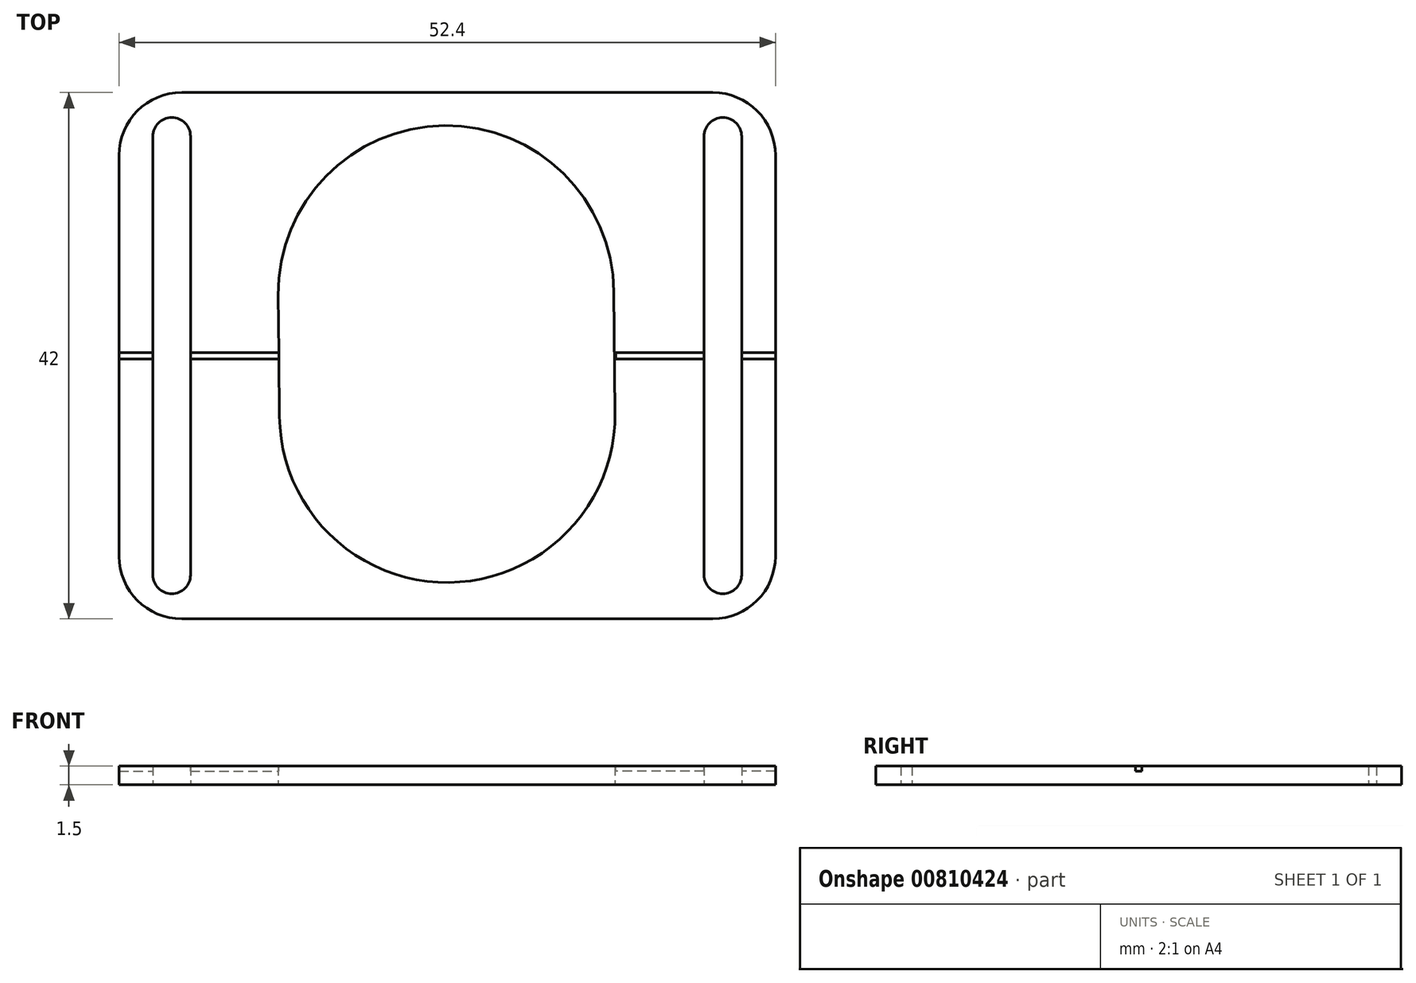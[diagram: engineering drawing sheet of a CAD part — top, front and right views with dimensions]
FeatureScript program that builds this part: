
annotation { "Feature Type Name" : "Feature", "Feature Type Description" : "" }
export const myFeature = defineFeature(function(context is Context, id is Id, definition is map)
    precondition{}
    {
        {
            var Q0;
            Q0=qCreatedBy(makeId("Top.planeOp"),FACE);
            var sketch = newSketch(context, id + "F0", { "sketchPlane" : qUnion([Q0])});
            skPoint(sketch, "E0.0", {"position": v(-35, -49.5) * mm});
            skPoint(sketch, "E1.0", {"position": v(35, -49.5) * mm});
            skLineSegment(sketch, "E2", {"start": v(-35, 25.5) * mm, "end": v(35, 25.5) * mm, "construction": true});
            skLineSegment(sketch, "E3.bottom", {"start": v(-32, -49.5) * mm, "end": v(-22, -49.5) * mm});
            skLineSegment(sketch, "E3.left", {"start": v(-35, -46.5) * mm, "end": v(-35, -44.8) * mm});
            skLineSegment(sketch, "E3.right", {"start": v(-19, -46.5) * mm, "end": v(-19, -45.44) * mm});
            skLineSegment(sketch, "E4.bottom", {"start": v(32, -49.5) * mm, "end": v(22, -49.5) * mm});
            skLineSegment(sketch, "E4.left", {"start": v(35, -46.5) * mm, "end": v(35, -44.8) * mm});
            skLineSegment(sketch, "E4.right", {"start": v(19, -46.5) * mm, "end": v(19, -45.44) * mm});
            skPoint(sketch, "E5.0", {"position": v(-19.7, -19.3) * mm});
            skPoint(sketch, "E6.0", {"position": v(19.7, -19.3) * mm});
            skArc(sketch, "E7", {"start": v(-30.65, -39.5) * mm, "mid": v(-31.62, -41.02) * mm, "end": v(-33.12, -42.02) * mm});
            skLineSegment(sketch, "E8", {"start": v(-18.8, -44.37) * mm, "end": v(-13.23, -29.76) * mm});
            skPoint(sketch, "E9.MirrorP", {"position": v(19.2, -19.2) * mm});
            skArc(sketch, "E10.MirrorCS", {"start": v(30.65, -39.5) * mm, "mid": v(31.62, -41.02) * mm, "end": v(33.12, -42.02) * mm});
            skLineSegment(sketch, "E11.MirrorCS", {"start": v(18.8, -44.37) * mm, "end": v(13.23, -29.76) * mm});
            skPoint(sketch, "E12.orphan", {"position": v(19, -39.5) * mm});
            skPoint(sketch, "E13.orphan", {"position": v(-19, -39.5) * mm});
            skPoint(sketch, "E14.visualSharp", {"position": v(-35, -42.32) * mm});
            skArc(sketch, "E14.filletArc", {"start": v(-33.12, -42.02) * mm, "mid": v(-34.48, -43.12) * mm, "end": v(-35, -44.8) * mm});
            skPoint(sketch, "E15.visualSharp", {"position": v(35, -42.32) * mm});
            skArc(sketch, "E15.filletArc", {"start": v(35, -44.8) * mm, "mid": v(34.48, -43.12) * mm, "end": v(33.12, -42.02) * mm});
            skArc(sketch, "E16.filletArc", {"start": v(32, -49.5) * mm, "mid": v(34.12, -48.62) * mm, "end": v(35, -46.5) * mm});
            skPoint(sketch, "E17.visualSharp", {"position": v(19, -49.5) * mm});
            skArc(sketch, "E17.filletArc", {"start": v(19, -46.5) * mm, "mid": v(19.88, -48.62) * mm, "end": v(22, -49.5) * mm});
            skPoint(sketch, "E18.visualSharp", {"position": v(-19, -49.5) * mm});
            skArc(sketch, "E18.filletArc", {"start": v(-22, -49.5) * mm, "mid": v(-19.88, -48.62) * mm, "end": v(-19, -46.5) * mm});
            skArc(sketch, "E19.filletArc", {"start": v(-35, -46.5) * mm, "mid": v(-34.12, -48.62) * mm, "end": v(-32, -49.5) * mm});
            skPoint(sketch, "E20.visualSharp", {"position": v(-19, -44.89) * mm});
            skArc(sketch, "E20.filletArc", {"start": v(-18.8, -44.37) * mm, "mid": v(-18.95, -44.9) * mm, "end": v(-19, -45.44) * mm});
            skPoint(sketch, "E21.visualSharp", {"position": v(19, -44.89) * mm});
            skArc(sketch, "E21.filletArc", {"start": v(19, -45.44) * mm, "mid": v(18.95, -44.9) * mm, "end": v(18.8, -44.37) * mm});
            skPoint(sketch, "E22.0", {"position": v(-32, 22.5) * mm});
            skPoint(sketch, "E23.0", {"position": v(-22, 22.5) * mm});
            skPoint(sketch, "E24.0", {"position": v(22, 22.5) * mm});
            skPoint(sketch, "E25.0", {"position": v(32, 22.5) * mm});
            skLineSegment(sketch, "E26.bottom", {"start": v(-32, 25.5) * mm, "end": v(-22, 25.5) * mm});
            skLineSegment(sketch, "E26.left", {"start": v(-35, 22.32) * mm, "end": v(-34.9, 20.58) * mm});
            skArc(sketch, "E27.filletArc", {"start": v(-34.9, 20.58) * mm, "mid": v(-34.34, 19.02) * mm, "end": v(-33.05, 18) * mm});
            skArc(sketch, "E28.filletArc", {"start": v(-32, 25.5) * mm, "mid": v(-34.18, 24.56) * mm, "end": v(-35, 22.32) * mm});
            skArc(sketch, "E29.filletArc", {"start": v(-19.63, 24.33) * mm, "mid": v(-20.68, 25.19) * mm, "end": v(-22, 25.5) * mm});
            skLineSegment(sketch, "E30", {"start": v(-33.05, 18) * mm, "end": v(-29.27, 16.41) * mm});
            skLineSegment(sketch, "E31.MirrorCS", {"start": v(35, 22.32) * mm, "end": v(34.9, 20.58) * mm});
            skArc(sketch, "E32.MirrorCS", {"start": v(19.63, 24.33) * mm, "mid": v(20.68, 25.19) * mm, "end": v(22, 25.5) * mm});
            skArc(sketch, "E33.MirrorCS", {"start": v(34.9, 20.58) * mm, "mid": v(34.34, 19.02) * mm, "end": v(33.05, 18) * mm});
            skArc(sketch, "E34.MirrorCS", {"start": v(32, 25.5) * mm, "mid": v(34.18, 24.56) * mm, "end": v(35, 22.32) * mm});
            skLineSegment(sketch, "E35.MirrorCS", {"start": v(32, 25.5) * mm, "end": v(22, 25.5) * mm});
            skLineSegment(sketch, "E36.MirrorCS", {"start": v(33.05, 18) * mm, "end": v(29.27, 16.41) * mm});
            skLineSegment(sketch, "E37", {"start": v(-15.68, 22.4) * mm, "end": v(15.68, 22.4) * mm});
            skLineSegment(sketch, "E38", {"start": v(-26.2, -26.85) * mm, "end": v(-26.2, 11.8) * mm});
            skLineSegment(sketch, "E39", {"start": v(-32, 22.5) * mm, "end": v(-22, 22.5) * mm, "construction": true});
            skCircle(sketch, "E40", {"center": v(-32, 22.5) * mm, "radius": 1.5 * mm});
            skCircle(sketch, "E41", {"center": v(32, 22.5) * mm, "radius": 1.5 * mm});
            skCircle(sketch, "E42", {"center": v(-32, -46.5) * mm, "radius": 1.5 * mm});
            skCircle(sketch, "E43", {"center": v(-22, -46.5) * mm, "radius": 1.5 * mm});
            skCircle(sketch, "E44", {"center": v(22, -46.5) * mm, "radius": 1.5 * mm});
            skCircle(sketch, "E45", {"center": v(32, -46.5) * mm, "radius": 1.5 * mm});
            skCircle(sketch, "E46", {"center": v(-22, 22.5) * mm, "radius": 1.5 * mm});
            skCircle(sketch, "E47", {"center": v(22, 22.5) * mm, "radius": 1.5 * mm});
            skCircle(sketch, "E48.0", {"center": v(-22, 0) * mm, "radius": 1.5 * mm, "construction": true});
            skCircle(sketch, "E49.0", {"center": v(-22, 10) * mm, "radius": 1.5 * mm, "construction": true});
            skCircle(sketch, "E50.0", {"center": v(-22, -10) * mm, "radius": 1.5 * mm, "construction": true});
            skArc(sketch, "E51.0.1.0", {"start": v(-23.5, -17.5) * mm, "mid": v(-22, -19) * mm, "end": v(-20.5, -17.5) * mm});
            skLineSegment(sketch, "E51.direction1", {"start": v(-22, -10) * mm, "end": v(3, -10) * mm, "construction": true});
            skLineSegment(sketch, "E51.direction2", {"start": v(-22, -10) * mm, "end": v(-22, -17.5) * mm, "construction": true});
            skArc(sketch, "E52.0.1.0", {"start": v(-20.5, 17.5) * mm, "mid": v(-22, 19) * mm, "end": v(-23.5, 17.5) * mm});
            skLineSegment(sketch, "E52.direction1", {"start": v(-22, 10) * mm, "end": v(3, 10) * mm, "construction": true});
            skLineSegment(sketch, "E52.direction2", {"start": v(-22, 10) * mm, "end": v(-22, 17.5) * mm, "construction": true});
            skLineSegment(sketch, "E53", {"start": v(-20.5, 17.5) * mm, "end": v(-20.5, -17.5) * mm});
            skLineSegment(sketch, "E54", {"start": v(-23.5, 17.5) * mm, "end": v(-23.5, -17.5) * mm});
            skArc(sketch, "E55.trimOffspring", {"start": v(-21.84, -16) * mm, "mid": v(-21.92, -16) * mm, "end": v(-22, -16) * mm});
            skLineSegment(sketch, "E56", {"start": v(-10.5, -26.94) * mm, "end": v(-3.06, -23.82) * mm});
            skLineSegment(sketch, "E57", {"start": v(3.15, -23.82) * mm, "end": v(10.5, -26.93) * mm});
            skPoint(sketch, "E58.orphan", {"position": v(-10.37, -22.5) * mm});
            skPoint(sketch, "E59.end.orphan", {"position": v(10.47, -22.53) * mm});
            skPoint(sketch, "E60.visualSharp", {"position": v(0.05, -22.51) * mm});
            skArc(sketch, "E60.filletArc", {"start": v(3.15, -23.82) * mm, "mid": v(0.05, -23.2) * mm, "end": v(-3.06, -23.82) * mm});
            skPoint(sketch, "E61.orphan", {"position": v(-26.2, 16.8) * mm});
            skPoint(sketch, "E62.trimOffspring.end.orphan", {"position": v(-19.2, 12.2) * mm});
            skLineSegment(sketch, "E63.trimOffspring", {"start": v(-26.52, -28.62) * mm, "end": v(-30.65, -39.5) * mm});
            skPoint(sketch, "E64.start.orphan", {"position": v(-19.2, -9.3) * mm});
            skPoint(sketch, "E65.trimOffspring.end.orphan", {"position": v(-9.7, -19.2) * mm});
            skPoint(sketch, "E66.orphan", {"position": v(9.2, -19.2) * mm});
            skLineSegment(sketch, "E67.MirrorCS", {"start": v(26.2, -26.85) * mm, "end": v(26.2, 11.8) * mm});
            skCircle(sketch, "E68.MirrorC", {"center": v(22, 10) * mm, "radius": 1.5 * mm, "construction": true});
            skLineSegment(sketch, "E69.MirrorCS", {"start": v(23.5, 17.5) * mm, "end": v(23.5, -17.5) * mm});
            skLineSegment(sketch, "E70.MirrorCS", {"start": v(22, -10) * mm, "end": v(22, -17.5) * mm, "construction": true});
            skLineSegment(sketch, "E71.MirrorCS", {"start": v(22, 10) * mm, "end": v(22, 17.5) * mm, "construction": true});
            skCircle(sketch, "E72.MirrorC", {"center": v(22, -10) * mm, "radius": 1.5 * mm, "construction": true});
            skArc(sketch, "E73.MirrorCS", {"start": v(20.5, 17.5) * mm, "mid": v(22, 19) * mm, "end": v(23.5, 17.5) * mm});
            skArc(sketch, "E74.MirrorCS", {"start": v(23.5, -17.5) * mm, "mid": v(22, -19) * mm, "end": v(20.5, -17.5) * mm});
            skLineSegment(sketch, "E75.MirrorCS", {"start": v(20.5, 17.5) * mm, "end": v(20.5, -17.5) * mm});
            skCircle(sketch, "E76.MirrorC", {"center": v(22, 0) * mm, "radius": 1.5 * mm, "construction": true});
            skLineSegment(sketch, "E77.trimOffspring", {"start": v(26.52, -28.62) * mm, "end": v(30.65, -39.5) * mm});
            skPoint(sketch, "E78.MirrorCS.end.orphan", {"position": v(22, -16) * mm});
            skPoint(sketch, "E78.MirrorCS.start.orphan", {"position": v(21.84, -16) * mm});
            skPoint(sketch, "E79.end.orphan", {"position": v(19.2, 12.2) * mm});
            skPoint(sketch, "E79.start.orphan", {"position": v(19.2, -9.2) * mm});
            skPoint(sketch, "E80.MirrorCS.end.orphan", {"position": v(19, 19.2) * mm});
            skPoint(sketch, "E81.MirrorCS.end.orphan", {"position": v(19, 21.46) * mm});
            skPoint(sketch, "E82.end.orphan", {"position": v(-19, 19.2) * mm});
            skPoint(sketch, "E26.right.end.orphan", {"position": v(-19, 21.46) * mm});
            skPoint(sketch, "E83.visualSharp", {"position": v(-26.2, -27.76) * mm});
            skArc(sketch, "E83.filletArc", {"start": v(-26.52, -28.62) * mm, "mid": v(-26.28, -27.75) * mm, "end": v(-26.2, -26.85) * mm});
            skPoint(sketch, "E84.visualSharp", {"position": v(26.2, -27.76) * mm});
            skArc(sketch, "E84.filletArc", {"start": v(26.2, -26.85) * mm, "mid": v(26.28, -27.75) * mm, "end": v(26.52, -28.62) * mm});
            skPoint(sketch, "E85.visualSharp", {"position": v(-12.47, -27.76) * mm});
            skArc(sketch, "E85.filletArc", {"start": v(-10.5, -26.94) * mm, "mid": v(-12.15, -28.07) * mm, "end": v(-13.23, -29.76) * mm});
            skPoint(sketch, "E86.visualSharp", {"position": v(12.47, -27.76) * mm});
            skArc(sketch, "E86.filletArc", {"start": v(13.23, -29.76) * mm, "mid": v(12.15, -28.07) * mm, "end": v(10.5, -26.93) * mm});
            skPoint(sketch, "E87.visualSharp", {"position": v(-19, 22.4) * mm});
            skArc(sketch, "E87.filletArc", {"start": v(-19.63, 24.33) * mm, "mid": v(-17.88, 22.9) * mm, "end": v(-15.68, 22.4) * mm});
            skPoint(sketch, "E88.visualSharp", {"position": v(19, 22.4) * mm});
            skArc(sketch, "E88.filletArc", {"start": v(15.68, 22.4) * mm, "mid": v(17.88, 22.9) * mm, "end": v(19.63, 24.33) * mm});
            skPoint(sketch, "E89.visualSharp", {"position": v(26.2, 15.13) * mm});
            skArc(sketch, "E89.filletArc", {"start": v(29.27, 16.41) * mm, "mid": v(27.04, 14.57) * mm, "end": v(26.2, 11.8) * mm});
            skPoint(sketch, "E90.visualSharp", {"position": v(-26.2, 15.13) * mm});
            skArc(sketch, "E90.filletArc", {"start": v(-26.2, 11.8) * mm, "mid": v(-27.04, 14.57) * mm, "end": v(-29.27, 16.41) * mm});
            skPoint(sketch, "E91.0", {"position": v(0, 0) * mm});
            skLineSegment(sketch, "E92.bottom", {"start": v(18.2, -18.2) * mm, "end": v(-18.2, -18.2) * mm});
            skLineSegment(sketch, "E92.top", {"start": v(18.2, 18.2) * mm, "end": v(-18.2, 18.2) * mm});
            skLineSegment(sketch, "E92.left", {"start": v(18.2, -18.2) * mm, "end": v(18.2, 18.2) * mm});
            skLineSegment(sketch, "E92.right", {"start": v(-18.2, -18.2) * mm, "end": v(-18.2, 18.2) * mm});
            skLineSegment(sketch, "E93.bottom", {"start": v(19.2, -19.2) * mm, "end": v(-19.2, -19.2) * mm});
            skLineSegment(sketch, "E93.top", {"start": v(19.2, 19.2) * mm, "end": v(-19.2, 19.2) * mm});
            skLineSegment(sketch, "E93.left", {"start": v(19.2, -19.2) * mm, "end": v(19.2, 19.2) * mm});
            skLineSegment(sketch, "E93.right", {"start": v(-19.2, -19.2) * mm, "end": v(-19.2, 19.2) * mm});
            skSolve(sketch);
        }
        {
            var Q0;
            Q0=qCreatedBy(makeId("Top.planeOp"),FACE);
            var sketch = newSketch(context, id + "F1", { "sketchPlane" : qUnion([Q0])});
            skCircle(sketch, "E94", {"center": v(0, 0) * mm, "radius": 12.4 * mm, "construction": true});
            skLineSegment(sketch, "E95.bottom", {"start": v(2.5, -22.4) * mm, "end": v(-2.5, -22.4) * mm, "construction": true});
            skLineSegment(sketch, "E95.top", {"start": v(2.5, 22.4) * mm, "end": v(-2.5, 22.4) * mm, "construction": true});
            skPoint(sketch, "E96", {"position": v(-22, 10) * mm});
            skCircle(sketch, "E97", {"center": v(-22, 10) * mm, "radius": 1.5 * mm, "construction": true});
            skArc(sketch, "E98.1.0.0", {"start": v(-16.7, 8.5) * mm, "mid": v(-15.2, 10) * mm, "end": v(-16.7, 11.5) * mm, "construction": true});
            skLineSegment(sketch, "E98.direction1", {"start": v(-22, 10) * mm, "end": v(-16.7, 10) * mm, "construction": true});
            skArc(sketch, "E99.1.0.0", {"start": v(-27, 11.5) * mm, "mid": v(-28.5, 10) * mm, "end": v(-27, 8.5) * mm, "construction": true});
            skLineSegment(sketch, "E99.direction1", {"start": v(-22, 10) * mm, "end": v(-27, 10) * mm, "construction": true});
            skLineSegment(sketch, "E100", {"start": v(-27, 11.5) * mm, "end": v(-16.7, 11.5) * mm, "construction": true});
            skLineSegment(sketch, "E101", {"start": v(-27, 8.5) * mm, "end": v(-16.7, 8.5) * mm, "construction": true});
            skLineSegment(sketch, "E102.direction2", {"start": v(-27, 8.5) * mm, "end": v(-27, -11.5) * mm, "construction": true});
            skPoint(sketch, "E103.visualSharp", {"position": v(-30.53, 22.4) * mm});
            skLineSegment(sketch, "E104", {"start": v(-22, 10) * mm, "end": v(-22, -10) * mm, "construction": true});
            skCircle(sketch, "E105", {"center": v(-22, 0) * mm, "radius": 1.5 * mm, "construction": true});
            skArc(sketch, "E106", {"start": v(-15.64, 4.24) * mm, "mid": v(-15.64, 6.36) * mm, "end": v(-17.76, 6.36) * mm, "construction": true});
            skLineSegment(sketch, "E107", {"start": v(-16.7, 5.3) * mm, "end": v(-22, 0) * mm, "construction": true});
            skLineSegment(sketch, "E108", {"start": v(-22, 0) * mm, "end": v(-25.5, 3.5) * mm, "construction": true});
            skArc(sketch, "E109.MirrorC", {"start": v(-26.24, -6.36) * mm, "mid": v(-28.36, -6.36) * mm, "end": v(-28.36, -4.24) * mm, "construction": true});
            skArc(sketch, "E110.MirrorC", {"start": v(-15.64, -4.24) * mm, "mid": v(-15.64, -6.36) * mm, "end": v(-17.76, -6.36) * mm, "construction": true});
            skArc(sketch, "E111.MirrorC", {"start": v(-28.36, 4.24) * mm, "mid": v(-28.36, 6.36) * mm, "end": v(-26.24, 6.36) * mm, "construction": true});
            skLineSegment(sketch, "E112", {"start": v(-26.24, 6.36) * mm, "end": v(-22.14, 2.26) * mm, "construction": true});
            skLineSegment(sketch, "E113", {"start": v(-17.76, 6.36) * mm, "end": v(-21.86, 2.26) * mm, "construction": true});
            skLineSegment(sketch, "E114.MirrorCS", {"start": v(-17.76, -6.36) * mm, "end": v(-21.86, -2.26) * mm, "construction": true});
            skLineSegment(sketch, "E115.MirrorCS", {"start": v(-26.24, -6.36) * mm, "end": v(-22.14, -2.26) * mm, "construction": true});
            skLineSegment(sketch, "E116.MirrorCS", {"start": v(-15.64, 4.24) * mm, "end": v(-19.74, 0.14) * mm, "construction": true});
            skLineSegment(sketch, "E117.MirrorCS", {"start": v(-28.36, 4.24) * mm, "end": v(-24.26, 0.14) * mm, "construction": true});
            skLineSegment(sketch, "E118.MirrorCS", {"start": v(-15.64, -4.24) * mm, "end": v(-19.74, -0.14) * mm, "construction": true});
            skLineSegment(sketch, "E119.MirrorCS", {"start": v(-28.36, -4.24) * mm, "end": v(-24.26, -0.14) * mm, "construction": true});
            skPoint(sketch, "E120.visualSharp", {"position": v(-24.12, 0) * mm});
            skArc(sketch, "E120.filletArc", {"start": v(-24.26, -0.14) * mm, "mid": v(-24.2, 0) * mm, "end": v(-24.26, 0.14) * mm, "construction": true});
            skPoint(sketch, "E121.visualSharp", {"position": v(-22, 2.12) * mm});
            skArc(sketch, "E121.filletArc", {"start": v(-22.14, 2.26) * mm, "mid": v(-22, 2.2) * mm, "end": v(-21.86, 2.26) * mm, "construction": true});
            skPoint(sketch, "E122.visualSharp", {"position": v(-19.88, 0) * mm});
            skArc(sketch, "E122.filletArc", {"start": v(-19.74, 0.14) * mm, "mid": v(-19.8, 0) * mm, "end": v(-19.74, -0.14) * mm, "construction": true});
            skPoint(sketch, "E123.visualSharp", {"position": v(-22, -2.12) * mm});
            skArc(sketch, "E123.filletArc", {"start": v(-21.86, -2.26) * mm, "mid": v(-22, -2.2) * mm, "end": v(-22.14, -2.26) * mm, "construction": true});
            skLineSegment(sketch, "E124.bottom", {"start": v(27, 13.5) * mm, "end": v(18.65, 13.5) * mm, "construction": true});
            skLineSegment(sketch, "E124.left", {"start": v(30.5, 10) * mm, "end": v(30.5, -10) * mm, "construction": true});
            skLineSegment(sketch, "E124.right", {"start": v(-30.5, 10) * mm, "end": v(-30.5, -10) * mm, "construction": true});
            skArc(sketch, "E125.MirrorCS", {"start": v(22.14, 2.26) * mm, "mid": v(22, 2.2) * mm, "end": v(21.86, 2.26) * mm, "construction": true});
            skArc(sketch, "E126.MirrorCS", {"start": v(21.86, -2.26) * mm, "mid": v(22, -2.2) * mm, "end": v(22.14, -2.26) * mm, "construction": true});
            skArc(sketch, "E127.MirrorCS", {"start": v(19.74, 0.14) * mm, "mid": v(19.8, 0) * mm, "end": v(19.74, -0.14) * mm, "construction": true});
            skArc(sketch, "E128.MirrorCS", {"start": v(24.26, -0.14) * mm, "mid": v(24.2, 0) * mm, "end": v(24.26, 0.14) * mm, "construction": true});
            skPoint(sketch, "E129.MirrorP", {"position": v(24.12, 0) * mm});
            skLineSegment(sketch, "E130.MirrorCS", {"start": v(15.64, -4.24) * mm, "end": v(19.74, -0.14) * mm, "construction": true});
            skArc(sketch, "E131.MirrorCS", {"start": v(28.36, 4.24) * mm, "mid": v(28.36, 6.36) * mm, "end": v(26.24, 6.36) * mm, "construction": true});
            skPoint(sketch, "E132.MirrorP", {"position": v(22, -2.12) * mm});
            skPoint(sketch, "E133.MirrorP", {"position": v(22, 2.12) * mm});
            skLineSegment(sketch, "E134.MirrorCS", {"start": v(22, 0) * mm, "end": v(25.5, 3.5) * mm, "construction": true});
            skArc(sketch, "E135.MirrorCS", {"start": v(15.64, -4.24) * mm, "mid": v(15.64, -6.36) * mm, "end": v(17.76, -6.36) * mm, "construction": true});
            skLineSegment(sketch, "E136.MirrorCS", {"start": v(28.36, 4.24) * mm, "end": v(24.26, 0.14) * mm, "construction": true});
            skPoint(sketch, "E137.MirrorP", {"position": v(22, 10) * mm});
            skArc(sketch, "E138.MirrorCS", {"start": v(16.7, 8.5) * mm, "mid": v(15.2, 10) * mm, "end": v(16.7, 11.5) * mm, "construction": true});
            skArc(sketch, "E139.MirrorCS", {"start": v(27, 11.5) * mm, "mid": v(28.5, 10) * mm, "end": v(27, 8.5) * mm, "construction": true});
            skLineSegment(sketch, "E140.MirrorCS", {"start": v(27, 8.5) * mm, "end": v(16.7, 8.5) * mm, "construction": true});
            skLineSegment(sketch, "E141.MirrorCS", {"start": v(28.36, -4.24) * mm, "end": v(24.26, -0.14) * mm, "construction": true});
            skPoint(sketch, "E142.MirrorP", {"position": v(19.88, 0) * mm});
            skArc(sketch, "E143.MirrorCS", {"start": v(15.64, 4.24) * mm, "mid": v(15.64, 6.36) * mm, "end": v(17.76, 6.36) * mm, "construction": true});
            skLineSegment(sketch, "E144.MirrorCS", {"start": v(27, 8.5) * mm, "end": v(27, -11.5) * mm, "construction": true});
            skLineSegment(sketch, "E145.MirrorCS", {"start": v(15.64, 4.24) * mm, "end": v(19.74, 0.14) * mm, "construction": true});
            skArc(sketch, "E146.MirrorCS", {"start": v(26.24, -6.36) * mm, "mid": v(28.36, -6.36) * mm, "end": v(28.36, -4.24) * mm, "construction": true});
            skLineSegment(sketch, "E147.MirrorCS", {"start": v(22, 10) * mm, "end": v(16.7, 10) * mm, "construction": true});
            skLineSegment(sketch, "E148.MirrorCS", {"start": v(22, 10) * mm, "end": v(22, -10) * mm, "construction": true});
            skCircle(sketch, "E149.MirrorC", {"center": v(22, 10) * mm, "radius": 1.5 * mm, "construction": true});
            skLineSegment(sketch, "E150.MirrorCS", {"start": v(16.7, 5.3) * mm, "end": v(22, 0) * mm, "construction": true});
            skLineSegment(sketch, "E151.MirrorCS", {"start": v(17.76, -6.36) * mm, "end": v(21.86, -2.26) * mm, "construction": true});
            skCircle(sketch, "E152.MirrorC", {"center": v(22, 0) * mm, "radius": 1.5 * mm, "construction": true});
            skLineSegment(sketch, "E153.MirrorCS", {"start": v(27, 11.5) * mm, "end": v(16.7, 11.5) * mm, "construction": true});
            skLineSegment(sketch, "E154.MirrorCS", {"start": v(26.24, 6.36) * mm, "end": v(22.14, 2.26) * mm, "construction": true});
            skLineSegment(sketch, "E155.MirrorCS", {"start": v(22, 10) * mm, "end": v(27, 10) * mm, "construction": true});
            skLineSegment(sketch, "E156.MirrorCS", {"start": v(26.24, -6.36) * mm, "end": v(22.14, -2.26) * mm, "construction": true});
            skLineSegment(sketch, "E157.MirrorCS", {"start": v(17.76, 6.36) * mm, "end": v(21.86, 2.26) * mm, "construction": true});
            skFitSpline(sketch, "E158", {"points": [v(-18.65, 13.5) * mm, v(-13.06, 15.7) * mm, v(-10.09, 18.6) * mm, v(-2.5, 22.4) * mm], "startDerivative": vector(19.72, -0.07) * mm, "endDerivative": vector(26.63, 0) * mm, "construction": true});
            skFitSpline(sketch, "E159.MirrorCS", {"points": [v(18.65, 13.5) * mm, v(13.06, 15.7) * mm, v(10.09, 18.6) * mm, v(2.5, 22.4) * mm], "startDerivative": vector(-19.72, -0.07) * mm, "endDerivative": vector(-26.63, 0) * mm, "construction": true});
            skFitSpline(sketch, "E160.MirrorCS", {"points": [v(-18.65, -13.5) * mm, v(-13.06, -15.7) * mm, v(-10.09, -18.6) * mm, v(-2.5, -22.4) * mm], "startDerivative": vector(19.72, 0.07) * mm, "endDerivative": vector(26.63, 0) * mm, "construction": true});
            skFitSpline(sketch, "E161.MirrorCS", {"points": [v(18.65, -13.5) * mm, v(13.06, -15.7) * mm, v(10.09, -18.6) * mm, v(2.5, -22.4) * mm], "startDerivative": vector(-19.72, 0.07) * mm, "endDerivative": vector(-26.63, 0) * mm, "construction": true});
            skPoint(sketch, "E162.visualSharp", {"position": v(-30.5, -13.5) * mm});
            skArc(sketch, "E162.filletArc", {"start": v(-30.5, -10) * mm, "mid": v(-29.5, -12.45) * mm, "end": v(-27.07, -13.5) * mm, "construction": true});
            skArc(sketch, "E163.filletArc", {"start": v(-27.15, 13.5) * mm, "mid": v(-29.53, 12.42) * mm, "end": v(-30.5, 10) * mm, "construction": true});
            skPoint(sketch, "E164.visualSharp", {"position": v(30.5, -13.5) * mm});
            skArc(sketch, "E164.filletArc", {"start": v(27.08, -13.5) * mm, "mid": v(29.5, -12.45) * mm, "end": v(30.5, -10) * mm, "construction": true});
            skPoint(sketch, "E165.visualSharp", {"position": v(30.5, 13.5) * mm});
            skArc(sketch, "E165.filletArc", {"start": v(30.5, 10) * mm, "mid": v(29.47, 12.47) * mm, "end": v(27, 13.5) * mm, "construction": true});
            skCircle(sketch, "E166.MirrorC", {"center": v(22, -10) * mm, "radius": 1.5 * mm, "construction": true});
            skArc(sketch, "E167.MirrorCS", {"start": v(27, -11.5) * mm, "mid": v(28.5, -10) * mm, "end": v(27, -8.5) * mm, "construction": true});
            skLineSegment(sketch, "E168.MirrorCS", {"start": v(22, -10) * mm, "end": v(27, -10) * mm, "construction": true});
            skLineSegment(sketch, "E169.MirrorCS", {"start": v(27, -8.5) * mm, "end": v(16.7, -8.5) * mm, "construction": true});
            skLineSegment(sketch, "E170.MirrorCS", {"start": v(27, -11.5) * mm, "end": v(16.7, -11.5) * mm, "construction": true});
            skLineSegment(sketch, "E171.MirrorCS", {"start": v(22, -10) * mm, "end": v(16.7, -10) * mm, "construction": true});
            skArc(sketch, "E172.MirrorCS", {"start": v(16.7, -8.5) * mm, "mid": v(15.2, -10) * mm, "end": v(16.7, -11.5) * mm, "construction": true});
            skArc(sketch, "E173.MirrorCS", {"start": v(-27, -11.5) * mm, "mid": v(-28.5, -10) * mm, "end": v(-27, -8.5) * mm, "construction": true});
            skLineSegment(sketch, "E174.MirrorCS", {"start": v(-27, -11.5) * mm, "end": v(-16.7, -11.5) * mm, "construction": true});
            skLineSegment(sketch, "E175.MirrorCS", {"start": v(-27, -8.5) * mm, "end": v(-16.7, -8.5) * mm, "construction": true});
            skArc(sketch, "E176.MirrorCS", {"start": v(-16.7, -8.5) * mm, "mid": v(-15.2, -10) * mm, "end": v(-16.7, -11.5) * mm, "construction": true});
            skLineSegment(sketch, "E177.MirrorCS", {"start": v(-22, -10) * mm, "end": v(-27, -10) * mm, "construction": true});
            skLineSegment(sketch, "E178.MirrorCS", {"start": v(-22, -10) * mm, "end": v(-16.7, -10) * mm, "construction": true});
            skCircle(sketch, "E179.MirrorC", {"center": v(-22, -10) * mm, "radius": 1.5 * mm, "construction": true});
            skLineSegment(sketch, "E180", {"start": v(-27.15, 13.5) * mm, "end": v(-18.65, 13.5) * mm, "construction": true});
            skLineSegment(sketch, "E181", {"start": v(27.08, -13.5) * mm, "end": v(18.65, -13.5) * mm, "construction": true});
            skLineSegment(sketch, "E182", {"start": v(-27.07, -13.5) * mm, "end": v(-18.65, -13.5) * mm, "construction": true});
            skSolve(sketch);
        }
        {
            var Q0;
            Q0=qCreatedBy(makeId("Top.planeOp"),FACE);
            var sketch = newSketch(context, id + "F2", { "sketchPlane" : qUnion([Q0])});
            skLineSegment(sketch, "E183.0.0", {"start": v(-20.5, -17.5) * mm, "end": v(-20.5, 17.5) * mm});
            skArc(sketch, "E183.0.1", {"start": v(-20.5, 17.5) * mm, "mid": v(-22, 19) * mm, "end": v(-23.5, 17.5) * mm});
            skLineSegment(sketch, "E183.0.2", {"start": v(-23.5, 17.5) * mm, "end": v(-23.5, -17.5) * mm});
            skArc(sketch, "E183.0.3", {"start": v(-23.5, -17.5) * mm, "mid": v(-22, -19) * mm, "end": v(-20.5, -17.5) * mm});
            skArc(sketch, "E184.0.0", {"start": v(23.5, 17.5) * mm, "mid": v(22, 19) * mm, "end": v(20.5, 17.5) * mm});
            skLineSegment(sketch, "E184.0.1", {"start": v(20.5, 17.5) * mm, "end": v(20.5, -17.5) * mm});
            skArc(sketch, "E184.0.2", {"start": v(20.5, -17.5) * mm, "mid": v(22, -19) * mm, "end": v(23.5, -17.5) * mm});
            skLineSegment(sketch, "E184.0.3", {"start": v(23.5, -17.5) * mm, "end": v(23.5, 17.5) * mm});
            skLineSegment(sketch, "E185.bottom", {"start": v(21.2, 21) * mm, "end": v(-21.2, 21) * mm});
            skLineSegment(sketch, "E185.top", {"start": v(21.2, -21) * mm, "end": v(-21.2, -21) * mm});
            skLineSegment(sketch, "E185.left", {"start": v(26.2, 16) * mm, "end": v(26.2, -16) * mm});
            skLineSegment(sketch, "E185.right", {"start": v(-26.2, 16) * mm, "end": v(-26.2, -16) * mm});
            skPoint(sketch, "E185.middle", {"position": v(0, 0) * mm});
            skPoint(sketch, "E186.visualSharp", {"position": v(-26.2, 21) * mm});
            skArc(sketch, "E186.filletArc", {"start": v(-21.2, 21) * mm, "mid": v(-24.74, 19.54) * mm, "end": v(-26.2, 16) * mm});
            skPoint(sketch, "E187.visualSharp", {"position": v(26.2, 21) * mm});
            skArc(sketch, "E187.filletArc", {"start": v(26.2, 16) * mm, "mid": v(24.74, 19.54) * mm, "end": v(21.2, 21) * mm});
            skPoint(sketch, "E188.visualSharp", {"position": v(26.2, -21) * mm});
            skArc(sketch, "E188.filletArc", {"start": v(21.2, -21) * mm, "mid": v(24.74, -19.54) * mm, "end": v(26.2, -16) * mm});
            skPoint(sketch, "E189.visualSharp", {"position": v(-26.2, -21) * mm});
            skArc(sketch, "E189.filletArc", {"start": v(-26.2, -16) * mm, "mid": v(-24.74, -19.54) * mm, "end": v(-21.2, -21) * mm});
            skCircle(sketch, "E190.0", {"center": v(0, 0) * mm, "radius": 12.4 * mm, "construction": true});
            skCircle(sketch, "E191", {"center": v(0, 0) * mm, "radius": 13.4 * mm, "construction": true});
            skArc(sketch, "E192", {"start": v(13.3, 5.1) * mm, "mid": v(-0.24, 18.36) * mm, "end": v(-13.5, 4.82) * mm});
            skArc(sketch, "E193", {"start": v(-13.4, -4.84) * mm, "mid": v(0.14, -18.1) * mm, "end": v(13.4, -4.56) * mm});
            skLineSegment(sketch, "E194", {"start": v(-13.5, 4.82) * mm, "end": v(-13.4, -4.84) * mm});
            skLineSegment(sketch, "E195", {"start": v(13.3, 5.1) * mm, "end": v(13.4, -4.56) * mm});
            skSolve(sketch);
        }
        {
            var Q0;
            Q0=makeQuery(id+"F2.imprint","IMPRINT",FACE,{"disambiguationData":[TD([[makeQuery(id+"F2.imprint","IMPRINT",EDGE,{"derivedFrom":sQuery(id+"F2.wireOp",EDGE,"E183.0.0")}),-1.0]])]});
            extrude(context, id + "F3", {"entities" : qUnion([Q0]), "depth" : 1.5 * mm});
        }
        {
            var Q0;
            Q0=makeQuery(id+"F3.opExtrude","CAP_FACE",FACE,{"disambiguationData":[OSD([sQuery(id+"F2.wireOp",EDGE,"E183.0.0"),sQuery(id+"F2.wireOp",EDGE,"E183.0.1"),sQuery(id+"F2.wireOp",EDGE,"E183.0.2"),sQuery(id+"F2.wireOp",EDGE,"E183.0.3"),sQuery(id+"F2.wireOp",EDGE,"E184.0.0"),sQuery(id+"F2.wireOp",EDGE,"E184.0.1"),sQuery(id+"F2.wireOp",EDGE,"E184.0.2"),sQuery(id+"F2.wireOp",EDGE,"E184.0.3"),sQuery(id+"F2.wireOp",EDGE,"E185.bottom"),sQuery(id+"F2.wireOp",EDGE,"E185.top"),sQuery(id+"F2.wireOp",EDGE,"E185.left"),sQuery(id+"F2.wireOp",EDGE,"E185.right"),sQuery(id+"F2.wireOp",EDGE,"E186.filletArc"),sQuery(id+"F2.wireOp",EDGE,"E187.filletArc"),sQuery(id+"F2.wireOp",EDGE,"E188.filletArc"),sQuery(id+"F2.wireOp",EDGE,"E189.filletArc"),sQuery(id+"F2.wireOp",EDGE,"E192"),sQuery(id+"F2.wireOp",EDGE,"E193"),sQuery(id+"F2.wireOp",EDGE,"E194"),sQuery(id+"F2.wireOp",EDGE,"E195")])],"isStart":false});
            var sketch = newSketch(context, id + "F4", { "sketchPlane" : qUnion([Q0])});
            skLineSegment(sketch, "E196.bottom", {"start": v(-26.2, 0.25) * mm, "end": v(-13.45, 0.25) * mm});
            skLineSegment(sketch, "E196.top", {"start": v(-26.2, -0.25) * mm, "end": v(-13.45, -0.25) * mm});
            skLineSegment(sketch, "E196.left", {"start": v(-26.2, 0.25) * mm, "end": v(-26.2, -0.25) * mm});
            skLineSegment(sketch, "E196.right", {"start": v(-13.45, 0.25) * mm, "end": v(-13.45, -0.25) * mm});
            skLineSegment(sketch, "E197.MirrorCS", {"start": v(13.45, 0.25) * mm, "end": v(13.45, -0.25) * mm});
            skLineSegment(sketch, "E198.MirrorCS", {"start": v(26.2, 0.25) * mm, "end": v(26.2, -0.25) * mm});
            skLineSegment(sketch, "E199.MirrorCS", {"start": v(26.2, 0.25) * mm, "end": v(13.45, 0.25) * mm});
            skLineSegment(sketch, "E200.MirrorCS", {"start": v(26.2, -0.25) * mm, "end": v(13.45, -0.25) * mm});
            skSolve(sketch);
        }
        {
            var Q0;
            Q0=qSketchRegion(id+"F4",true);
            extrude(context, id + "F5", {"entities" : qUnion([Q0]), "operationType" : NewBodyOperationType.REMOVE, "oppositeDirection" : true, "depth" : 0.4 * mm, "offsetDistance" : 25 * mm});
        }
    });
